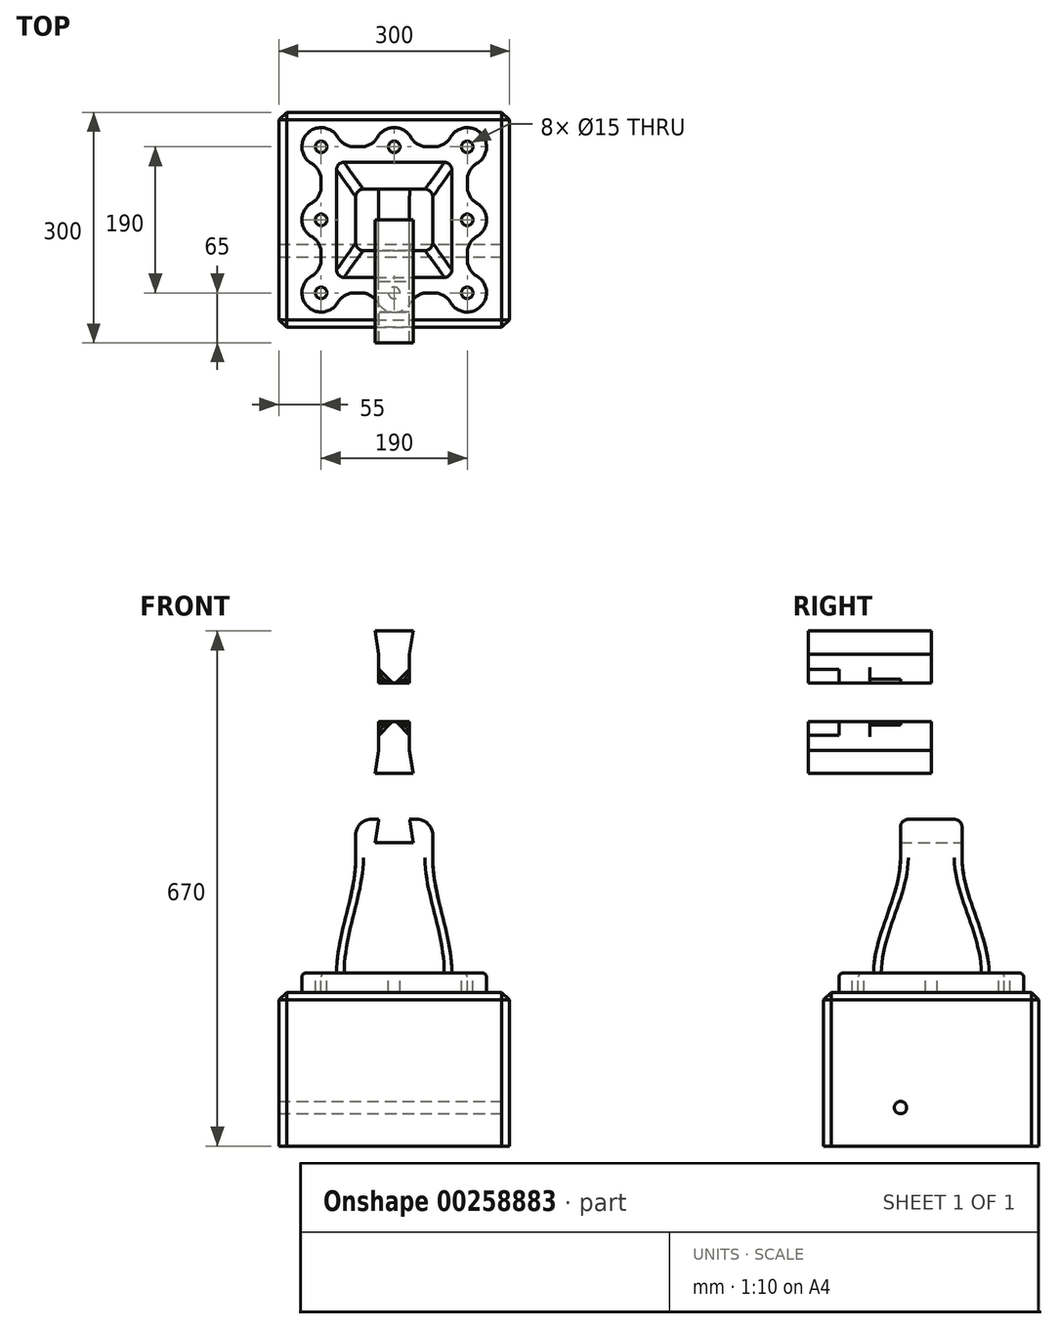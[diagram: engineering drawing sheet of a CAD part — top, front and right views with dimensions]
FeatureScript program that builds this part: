
annotation { "Feature Type Name" : "Feature", "Feature Type Description" : "" }
export const myFeature = defineFeature(function(context is Context, id is Id, definition is map)
    precondition{}
    {
        {
            var Q0;
            Q0=qCreatedBy(makeId("Top.planeOp"),FACE);
            var sketch = newSketch(context, id + "F0", { "sketchPlane" : qUnion([Q0])});
            skLineSegment(sketch, "E0.bottom", {"start": v(-75, 75) * mm, "end": v(75, 75) * mm});
            skLineSegment(sketch, "E0.top", {"start": v(-75, -75) * mm, "end": v(75, -75) * mm});
            skLineSegment(sketch, "E0.left", {"start": v(-75, 75) * mm, "end": v(-75, -75) * mm});
            skLineSegment(sketch, "E0.right", {"start": v(75, 75) * mm, "end": v(75, -75) * mm});
            skPoint(sketch, "E0.middle", {"position": v(0, 0) * mm});
            skCircle(sketch, "E1", {"center": v(-95, 95) * mm, "radius": 7.5 * mm});
            skCircle(sketch, "E2", {"center": v(95, 95) * mm, "radius": 7.5 * mm});
            skCircle(sketch, "E3", {"center": v(95, 0) * mm, "radius": 7.5 * mm});
            skCircle(sketch, "E4", {"center": v(95, -95) * mm, "radius": 7.5 * mm});
            skCircle(sketch, "E5", {"center": v(-95, -95) * mm, "radius": 7.5 * mm});
            skCircle(sketch, "E6", {"center": v(-95, 0) * mm, "radius": 7.5 * mm});
            skArc(sketch, "E7", {"start": v(-107.5, -21.65) * mm, "mid": v(-120, 0) * mm, "end": v(-107.5, 21.65) * mm});
            skArc(sketch, "E8", {"start": v(-107.5, 73.35) * mm, "mid": v(-112.68, 112.68) * mm, "end": v(-73.35, 107.5) * mm});
            skArc(sketch, "E9", {"start": v(73.35, 107.5) * mm, "mid": v(112.68, 112.68) * mm, "end": v(107.5, 73.35) * mm});
            skArc(sketch, "E10", {"start": v(107.5, 21.65) * mm, "mid": v(120, 0) * mm, "end": v(107.5, -21.65) * mm});
            skArc(sketch, "E11", {"start": v(107.5, -73.35) * mm, "mid": v(112.68, -112.68) * mm, "end": v(73.35, -107.5) * mm});
            skArc(sketch, "E12", {"start": v(-73.35, -107.5) * mm, "mid": v(-112.68, -112.68) * mm, "end": v(-107.5, -73.35) * mm});
            skArc(sketch, "E13", {"start": v(-107.5, -73.35) * mm, "mid": v(-98.35, -64.2) * mm, "end": v(-95, -51.7) * mm});
            skLineSegment(sketch, "E14", {"start": v(-95, -51.7) * mm, "end": v(-95, -43.3) * mm});
            skArc(sketch, "E15", {"start": v(-95, -43.3) * mm, "mid": v(-98.35, -30.8) * mm, "end": v(-107.5, -21.65) * mm});
            skArc(sketch, "E16", {"start": v(-107.5, 21.65) * mm, "mid": v(-98.35, 30.8) * mm, "end": v(-95, 43.3) * mm});
            skArc(sketch, "E17", {"start": v(-95, 51.7) * mm, "mid": v(-98.35, 64.2) * mm, "end": v(-107.5, 73.35) * mm});
            skArc(sketch, "E18", {"start": v(-51.7, 95) * mm, "mid": v(-64.2, 98.35) * mm, "end": v(-73.35, 107.5) * mm});
            skArc(sketch, "E19", {"start": v(51.7, 95) * mm, "mid": v(64.2, 98.35) * mm, "end": v(73.35, 107.5) * mm});
            skArc(sketch, "E20", {"start": v(-51.7, -95) * mm, "mid": v(-64.2, -98.35) * mm, "end": v(-73.35, -107.5) * mm});
            skLineSegment(sketch, "E21", {"start": v(-95, 51.7) * mm, "end": v(-95, 43.3) * mm});
            skArc(sketch, "E22", {"start": v(73.35, -107.5) * mm, "mid": v(64.2, -98.35) * mm, "end": v(51.7, -95) * mm});
            skArc(sketch, "E23", {"start": v(95, 43.3) * mm, "mid": v(98.35, 30.8) * mm, "end": v(107.5, 21.65) * mm});
            skArc(sketch, "E24", {"start": v(107.5, 73.35) * mm, "mid": v(98.35, 64.2) * mm, "end": v(95, 51.7) * mm});
            skArc(sketch, "E25", {"start": v(95, -51.7) * mm, "mid": v(98.35, -64.2) * mm, "end": v(107.5, -73.35) * mm});
            skArc(sketch, "E26", {"start": v(107.5, -21.65) * mm, "mid": v(98.35, -30.8) * mm, "end": v(95, -43.3) * mm});
            skLineSegment(sketch, "E27", {"start": v(95, -51.7) * mm, "end": v(95, -43.3) * mm});
            skLineSegment(sketch, "E28", {"start": v(95, 43.3) * mm, "end": v(95, 51.7) * mm});
            skCircle(sketch, "E29", {"center": v(0, -95) * mm, "radius": 7.5 * mm});
            skCircle(sketch, "E30", {"center": v(0, 95) * mm, "radius": 7.5 * mm});
            skArc(sketch, "E31", {"start": v(-21.65, 107.5) * mm, "mid": v(0, 120) * mm, "end": v(21.65, 107.5) * mm});
            skArc(sketch, "E32", {"start": v(-43.3, 95) * mm, "mid": v(-30.8, 98.35) * mm, "end": v(-21.65, 107.5) * mm});
            skArc(sketch, "E33", {"start": v(21.65, 107.5) * mm, "mid": v(30.8, 98.35) * mm, "end": v(43.3, 95) * mm});
            skLineSegment(sketch, "E34", {"start": v(-51.7, 95) * mm, "end": v(-43.3, 95) * mm});
            skLineSegment(sketch, "E35", {"start": v(43.3, 95) * mm, "end": v(51.7, 95) * mm});
            skArc(sketch, "E36", {"start": v(-21.65, -107.5) * mm, "mid": v(0, -120) * mm, "end": v(21.65, -107.5) * mm});
            skArc(sketch, "E37", {"start": v(-21.65, -107.5) * mm, "mid": v(-30.8, -98.35) * mm, "end": v(-43.3, -95) * mm});
            skArc(sketch, "E38", {"start": v(43.3, -95) * mm, "mid": v(30.8, -98.35) * mm, "end": v(21.65, -107.5) * mm});
            skLineSegment(sketch, "E39", {"start": v(-51.7, -95) * mm, "end": v(-43.3, -95) * mm});
            skLineSegment(sketch, "E40", {"start": v(43.3, -95) * mm, "end": v(51.7, -95) * mm});
            skLineSegment(sketch, "E41.bottom", {"start": v(-150, 150) * mm, "end": v(150, 150) * mm});
            skLineSegment(sketch, "E41.top", {"start": v(-150, -150) * mm, "end": v(150, -150) * mm});
            skLineSegment(sketch, "E41.left", {"start": v(-150, 150) * mm, "end": v(-150, -150) * mm});
            skLineSegment(sketch, "E41.right", {"start": v(150, 150) * mm, "end": v(150, -150) * mm});
            skSolve(sketch);
        }
        {
            var Q0;
            Q0=qCreatedBy(makeId("Top.planeOp"),FACE);
            cPlane(context, id + "F1", {"entities" : qUnion([Q0]), "cplaneType" : CPlaneType.OFFSET, "offset" : 150 * mm, "width" : 150 * mm, "height" : 150 * mm});
        }
        {
            var Q0;
            Q0=qCreatedBy(id+"F1.planeOp",FACE);
            var sketch = newSketch(context, id + "F2", { "sketchPlane" : qUnion([Q0])});
            skLineSegment(sketch, "E42.bottom", {"start": v(-50, 40) * mm, "end": v(50, 40) * mm});
            skLineSegment(sketch, "E42.top", {"start": v(-50, -40) * mm, "end": v(50, -40) * mm});
            skLineSegment(sketch, "E42.left", {"start": v(-50, 40) * mm, "end": v(-50, -40) * mm});
            skLineSegment(sketch, "E42.right", {"start": v(50, 40) * mm, "end": v(50, -40) * mm});
            skPoint(sketch, "E42.middle", {"position": v(0, 0) * mm});
            skSolve(sketch);
        }
        {
            var Q0;
            Q0=makeQuery(id+"F2.imprint","IMPRINT",FACE,{"disambiguationData":[TD([[makeQuery(id+"F2.imprint","IMPRINT",EDGE,{"derivedFrom":sQuery(id+"F2.wireOp",EDGE,"E42.bottom")}),-1.0]])]});
            var Q1;
            Q1=makeQuery(id+"F0.imprint","IMPRINT",FACE,{"disambiguationData":[TD([[makeQuery(id+"F0.imprint","IMPRINT",EDGE,{"derivedFrom":sQuery(id+"F0.wireOp",EDGE,"E0.bottom")}),-1.0]])]});
            loft(context, id + "F3", {"startCondition" : LoftEndDerivativeType.NORMAL_TO_PROFILE, "startMagnitude" : 1, "endCondition" : LoftEndDerivativeType.NORMAL_TO_PROFILE, "endMagnitude" : 1, "sheetProfilesArray" : [{ "sheetProfileEntities" : qUnion([Q0]) }, { "sheetProfileEntities" : qUnion([Q1]) }]});
        }
        {
            var Q0;
            Q0=qCreatedBy(makeId("Front.planeOp"),FACE);
            var sketch = newSketch(context, id + "F4", { "sketchPlane" : qUnion([Q0])});
            skLineSegment(sketch, "E43", {"start": v(0, 150) * mm, "end": v(50, 150) * mm});
            skLineSegment(sketch, "E44", {"start": v(50, 150) * mm, "end": v(50, 200) * mm});
            skLineSegment(sketch, "E45", {"start": v(50, 200) * mm, "end": v(20, 200) * mm});
            skLineSegment(sketch, "E46", {"start": v(20, 200) * mm, "end": v(25, 170) * mm});
            skLineSegment(sketch, "E47", {"start": v(25, 170) * mm, "end": v(-25, 170) * mm});
            skLineSegment(sketch, "E48", {"start": v(-25, 170) * mm, "end": v(-20, 200) * mm});
            skLineSegment(sketch, "E49", {"start": v(-20, 200) * mm, "end": v(-50, 200) * mm});
            skLineSegment(sketch, "E50", {"start": v(-50, 200) * mm, "end": v(-50, 150) * mm});
            skLineSegment(sketch, "E51", {"start": v(-50, 150) * mm, "end": v(0, 150) * mm});
            skLineSegment(sketch, "E52", {"start": v(-25, 260) * mm, "end": v(25, 260) * mm});
            skLineSegment(sketch, "E53", {"start": v(25, 260) * mm, "end": v(20, 290) * mm});
            skLineSegment(sketch, "E54", {"start": v(20, 290) * mm, "end": v(-20, 290) * mm, "construction": true});
            skLineSegment(sketch, "E55", {"start": v(-20, 290) * mm, "end": v(-25, 260) * mm});
            skLineSegment(sketch, "E56", {"start": v(-20, 290) * mm, "end": v(-20, 307.5) * mm});
            skLineSegment(sketch, "E57", {"start": v(-20, 307.5) * mm, "end": v(20, 307.5) * mm, "construction": true});
            skLineSegment(sketch, "E58", {"start": v(20, 307.5) * mm, "end": v(20, 290) * mm});
            skLineSegment(sketch, "E59", {"start": v(-20, 290) * mm, "end": v(-70, 290) * mm});
            skLineSegment(sketch, "E60", {"start": v(-70, 290) * mm, "end": v(-70, 415) * mm});
            skLineSegment(sketch, "E61", {"start": v(-70, 415) * mm, "end": v(-20, 415) * mm});
            skLineSegment(sketch, "E62", {"start": v(-70, 352.5) * mm, "end": v(25, 352.5) * mm, "construction": true});
            skArc(sketch, "E63", {"start": v(20, 307.5) * mm, "mid": v(0, 327.5) * mm, "end": v(-20, 307.5) * mm});
            skPoint(sketch, "E64.visualSharp", {"position": v(0, 327.5) * mm});
            skLineSegment(sketch, "E65", {"start": v(-20, 307.5) * mm, "end": v(-20, 322.5) * mm});
            skLineSegment(sketch, "E66", {"start": v(20, 307.5) * mm, "end": v(20, 322.5) * mm});
            skLineSegment(sketch, "E67", {"start": v(20, 322.5) * mm, "end": v(20, 327.5) * mm});
            skLineSegment(sketch, "E68", {"start": v(20, 327.5) * mm, "end": v(-20, 327.5) * mm});
            skLineSegment(sketch, "E69", {"start": v(-20, 327.5) * mm, "end": v(-20, 322.5) * mm});
            skArc(sketch, "E70", {"start": v(20, 322.5) * mm, "mid": v(0, 327.5) * mm, "end": v(-20, 322.5) * mm});
            skArc(sketch, "E71", {"start": v(3.54, 326.04) * mm, "mid": v(0, 327.5) * mm, "end": v(-3.54, 326.04) * mm});
            skLineSegment(sketch, "E72", {"start": v(-3.54, 326.04) * mm, "end": v(-19.88, 309.7) * mm});
            skLineSegment(sketch, "E73", {"start": v(-19.88, 309.7) * mm, "end": v(19.88, 309.7) * mm, "construction": true});
            skLineSegment(sketch, "E74", {"start": v(19.88, 309.7) * mm, "end": v(3.54, 326.04) * mm});
            skLineSegment(sketch, "E75.MirrorCS", {"start": v(20, 382.5) * mm, "end": v(20, 377.5) * mm});
            skArc(sketch, "E76.MirrorCS", {"start": v(3.54, 378.96) * mm, "mid": v(0, 377.5) * mm, "end": v(-3.54, 378.96) * mm});
            skLineSegment(sketch, "E77.MirrorCS", {"start": v(-20, 377.5) * mm, "end": v(-20, 382.5) * mm});
            skPoint(sketch, "E78.MirrorP", {"position": v(0, 377.5) * mm});
            skLineSegment(sketch, "E79.MirrorCS", {"start": v(20, 415) * mm, "end": v(-20, 415) * mm, "construction": true});
            skLineSegment(sketch, "E80.MirrorCS", {"start": v(-20, 397.5) * mm, "end": v(20, 397.5) * mm, "construction": true});
            skArc(sketch, "E81.MirrorCS", {"start": v(20, 382.5) * mm, "mid": v(0, 377.5) * mm, "end": v(-20, 382.5) * mm});
            skLineSegment(sketch, "E82.MirrorCS", {"start": v(-20, 397.5) * mm, "end": v(-20, 382.5) * mm});
            skLineSegment(sketch, "E83.MirrorCS", {"start": v(20, 377.5) * mm, "end": v(-20, 377.5) * mm});
            skLineSegment(sketch, "E84.MirrorCS", {"start": v(-25, 445) * mm, "end": v(25, 445) * mm});
            skLineSegment(sketch, "E85.MirrorCS", {"start": v(-19.88, 395.3) * mm, "end": v(19.88, 395.3) * mm, "construction": true});
            skArc(sketch, "E86.MirrorCS", {"start": v(20, 397.5) * mm, "mid": v(0, 377.5) * mm, "end": v(-20, 397.5) * mm});
            skLineSegment(sketch, "E87.MirrorCS", {"start": v(-3.54, 378.96) * mm, "end": v(-19.88, 395.3) * mm});
            skLineSegment(sketch, "E88.MirrorCS", {"start": v(25, 445) * mm, "end": v(20, 415) * mm});
            skLineSegment(sketch, "E89.MirrorCS", {"start": v(-20, 415) * mm, "end": v(-20, 397.5) * mm});
            skLineSegment(sketch, "E90.MirrorCS", {"start": v(-20, 415) * mm, "end": v(-25, 445) * mm});
            skLineSegment(sketch, "E91.MirrorCS", {"start": v(20, 397.5) * mm, "end": v(20, 382.5) * mm});
            skLineSegment(sketch, "E92.MirrorCS", {"start": v(20, 397.5) * mm, "end": v(20, 415) * mm});
            skLineSegment(sketch, "E93.MirrorCS", {"start": v(19.88, 395.3) * mm, "end": v(3.54, 378.96) * mm});
            skSolve(sketch);
        }
        {
            var Q0;
            Q0=makeQuery(id+"F4.imprint","IMPRINT",FACE,{"disambiguationData":[TD([[makeQuery(id+"F4.imprint","IMPRINT",EDGE,{"derivedFrom":sQuery(id+"F4.wireOp",EDGE,"E43")}),1.0]])]});
            extrude(context, id + "F5", {"entities" : qUnion([Q0]), "operationType" : NewBodyOperationType.ADD, "depth" : 80 * mm, "symmetric" : true});
        }
        {
            var Q0;
            Q0=makeQuery(id+"F0.imprint","IMPRINT",FACE,{"disambiguationData":[TD([[makeQuery(id+"F0.imprint","IMPRINT",EDGE,{"derivedFrom":sQuery(id+"F0.wireOp",EDGE,"E0.bottom")}),-1.0]])]});
            var Q1;
            Q1=makeQuery(id+"F0.imprint","IMPRINT",FACE,{"disambiguationData":[TD([[makeQuery(id+"F0.imprint","IMPRINT",EDGE,{"derivedFrom":sQuery(id+"F0.wireOp",EDGE,"E0.bottom")}),1.0]])]});
            extrude(context, id + "F6", {"entities" : qUnion([Q0, Q1]), "operationType" : NewBodyOperationType.ADD, "oppositeDirection" : true, "depth" : 25 * mm});
        }
        {
            var Q0;
            Q0=makeQuery(id+"F5.opExtrude","SWEPT_EDGE",EDGE,{"disambiguationData":[OSD([sQuery(id+"F4.wireOp",EDGE,"E44"),sQuery(id+"F4.wireOp",EDGE,"E45")])]});
            var Q1;
            Q1=makeQuery(id+"F5.opExtrude","SWEPT_EDGE",EDGE,{"disambiguationData":[OSD([sQuery(id+"F4.wireOp",EDGE,"E49"),sQuery(id+"F4.wireOp",EDGE,"E50")])]});
            fillet(context, id + "F7", {"entities" : qUnion([Q0, Q1]), "radius" : 20 * mm, "tangentPropagation" : true, "allowEdgeOverflow" : false});
        }
        {
            var Q0;
            Q0=makeQuery(id+"F3.opLoft","SWEPT_EDGE",EDGE,{"disambiguationData":[OSD([sQuery(id+"F0.wireOp",EDGE,"E0.bottom"),sQuery(id+"F0.wireOp",EDGE,"E0.right"),sQuery(id+"F2.wireOp",EDGE,"E42.bottom"),sQuery(id+"F2.wireOp",EDGE,"E42.right")])]});
            var Q1;
            Q1=makeQuery(id+"F3.opLoft","SWEPT_EDGE",EDGE,{"disambiguationData":[OSD([sQuery(id+"F0.wireOp",EDGE,"E0.top"),sQuery(id+"F0.wireOp",EDGE,"E0.right"),sQuery(id+"F2.wireOp",EDGE,"E42.top"),sQuery(id+"F2.wireOp",EDGE,"E42.right")])]});
            var Q2;
            Q2=makeQuery(id+"F5.opExtrude","CAP_EDGE",EDGE,{"disambiguationData":[OSD([sQuery(id+"F4.wireOp",EDGE,"E49")])],"isStart":false});
            var Q3;
            Q3=makeQuery(id+"F3.opLoft","SWEPT_EDGE",EDGE,{"disambiguationData":[OSD([sQuery(id+"F0.wireOp",EDGE,"E0.bottom"),sQuery(id+"F0.wireOp",EDGE,"E0.left"),sQuery(id+"F2.wireOp",EDGE,"E42.bottom"),sQuery(id+"F2.wireOp",EDGE,"E42.left")])]});
            fillet(context, id + "F8", {"entities" : qUnion([Q0, Q1, Q2, Q3]), "radius" : 10 * mm, "tangentPropagation" : true, "allowEdgeOverflow" : false});
        }
        {
            var Q0;
            Q0=makeQuery(id+"F6.opExtrude","CAP_EDGE",EDGE,{"disambiguationData":[OSD([sQuery(id+"F0.wireOp",EDGE,"E27")])],"isStart":true});
            var Q1;
            Q1=makeQuery(id+"F3.opLoft","MID_CAP_EDGE",EDGE,{"disambiguationData":[OSD([sQuery(id+"F0.wireOp",EDGE,"E0.bottom"),sQuery(id+"F0.wireOp",EDGE,"E0.top"),sQuery(id+"F0.wireOp",EDGE,"E0.right")])],"capPos":1.0});
            fillet(context, id + "F9", {"entities" : qUnion([Q0, Q1]), "radius" : 5 * mm, "tangentPropagation" : true, "allowEdgeOverflow" : false});
        }
        {
            var Q0;
            Q0=qCreatedBy(makeId("Top.planeOp"),FACE);
            cPlane(context, id + "F10", {"entities" : qUnion([Q0]), "cplaneType" : CPlaneType.OFFSET, "offset" : 25 * mm, "oppositeDirection" : true, "width" : 150 * mm, "height" : 150 * mm});
        }
        {
            var Q0;
            Q0=qCreatedBy(id+"F10.planeOp",FACE);
            var sketch = newSketch(context, id + "F11", { "sketchPlane" : qUnion([Q0])});
            skArc(sketch, "E94.0.0", {"start": v(107.5, -21.65) * mm, "mid": v(98.35, -30.8) * mm, "end": v(95, -43.3) * mm});
            skLineSegment(sketch, "E94.0.1", {"start": v(95, -43.3) * mm, "end": v(95, -51.7) * mm});
            skArc(sketch, "E94.0.2", {"start": v(95, -51.7) * mm, "mid": v(98.35, -64.2) * mm, "end": v(107.5, -73.35) * mm});
            skArc(sketch, "E94.0.3", {"start": v(107.5, -73.35) * mm, "mid": v(112.68, -112.68) * mm, "end": v(73.35, -107.5) * mm});
            skArc(sketch, "E94.0.4", {"start": v(73.35, -107.5) * mm, "mid": v(64.2, -98.35) * mm, "end": v(51.7, -95) * mm});
            skLineSegment(sketch, "E94.0.5", {"start": v(51.7, -95) * mm, "end": v(43.3, -95) * mm});
            skArc(sketch, "E94.0.6", {"start": v(43.3, -95) * mm, "mid": v(30.8, -98.35) * mm, "end": v(21.65, -107.5) * mm});
            skArc(sketch, "E94.0.7", {"start": v(21.65, -107.5) * mm, "mid": v(0, -120) * mm, "end": v(-21.65, -107.5) * mm});
            skArc(sketch, "E94.0.8", {"start": v(-21.65, -107.5) * mm, "mid": v(-30.8, -98.35) * mm, "end": v(-43.3, -95) * mm});
            skLineSegment(sketch, "E94.0.9", {"start": v(-43.3, -95) * mm, "end": v(-51.7, -95) * mm});
            skArc(sketch, "E94.0.10", {"start": v(-51.7, -95) * mm, "mid": v(-64.2, -98.35) * mm, "end": v(-73.35, -107.5) * mm});
            skArc(sketch, "E94.0.11", {"start": v(-73.35, -107.5) * mm, "mid": v(-112.68, -112.68) * mm, "end": v(-107.5, -73.35) * mm});
            skArc(sketch, "E94.0.12", {"start": v(-107.5, -73.35) * mm, "mid": v(-98.35, -64.2) * mm, "end": v(-95, -51.7) * mm});
            skLineSegment(sketch, "E94.0.13", {"start": v(-95, -51.7) * mm, "end": v(-95, -43.3) * mm});
            skArc(sketch, "E94.0.14", {"start": v(-95, -43.3) * mm, "mid": v(-98.35, -30.8) * mm, "end": v(-107.5, -21.65) * mm});
            skArc(sketch, "E94.0.15", {"start": v(-107.5, -21.65) * mm, "mid": v(-120, 0) * mm, "end": v(-107.5, 21.65) * mm});
            skArc(sketch, "E94.0.16", {"start": v(-107.5, 21.65) * mm, "mid": v(-98.35, 30.8) * mm, "end": v(-95, 43.3) * mm});
            skLineSegment(sketch, "E94.0.17", {"start": v(-95, 43.3) * mm, "end": v(-95, 51.7) * mm});
            skArc(sketch, "E94.0.18", {"start": v(-95, 51.7) * mm, "mid": v(-98.35, 64.2) * mm, "end": v(-107.5, 73.35) * mm});
            skArc(sketch, "E94.0.19", {"start": v(-107.5, 73.35) * mm, "mid": v(-112.68, 112.68) * mm, "end": v(-73.35, 107.5) * mm});
            skArc(sketch, "E94.0.20", {"start": v(-73.35, 107.5) * mm, "mid": v(-64.2, 98.35) * mm, "end": v(-51.7, 95) * mm});
            skLineSegment(sketch, "E94.0.21", {"start": v(-51.7, 95) * mm, "end": v(-43.3, 95) * mm});
            skArc(sketch, "E94.0.22", {"start": v(-43.3, 95) * mm, "mid": v(-30.8, 98.35) * mm, "end": v(-21.65, 107.5) * mm});
            skArc(sketch, "E94.0.23", {"start": v(-21.65, 107.5) * mm, "mid": v(0, 120) * mm, "end": v(21.65, 107.5) * mm});
            skArc(sketch, "E94.0.24", {"start": v(21.65, 107.5) * mm, "mid": v(30.8, 98.35) * mm, "end": v(43.3, 95) * mm});
            skLineSegment(sketch, "E94.0.25", {"start": v(43.3, 95) * mm, "end": v(51.7, 95) * mm});
            skArc(sketch, "E94.0.26", {"start": v(51.7, 95) * mm, "mid": v(64.2, 98.35) * mm, "end": v(73.35, 107.5) * mm});
            skArc(sketch, "E94.0.27", {"start": v(73.35, 107.5) * mm, "mid": v(112.68, 112.68) * mm, "end": v(107.5, 73.35) * mm});
            skArc(sketch, "E94.0.28", {"start": v(107.5, 73.35) * mm, "mid": v(98.35, 64.2) * mm, "end": v(95, 51.7) * mm});
            skLineSegment(sketch, "E94.0.29", {"start": v(95, 51.7) * mm, "end": v(95, 43.3) * mm});
            skArc(sketch, "E94.0.30", {"start": v(95, 43.3) * mm, "mid": v(98.35, 30.8) * mm, "end": v(107.5, 21.65) * mm});
            skArc(sketch, "E94.0.31", {"start": v(107.5, 21.65) * mm, "mid": v(120, 0) * mm, "end": v(107.5, -21.65) * mm});
            skCircle(sketch, "E95.0", {"center": v(-95, 95) * mm, "radius": 7.5 * mm});
            skCircle(sketch, "E96.0", {"center": v(0, 95) * mm, "radius": 7.5 * mm});
            skCircle(sketch, "E97.0", {"center": v(95, 95) * mm, "radius": 7.5 * mm});
            skCircle(sketch, "E98.0", {"center": v(95, 0) * mm, "radius": 7.5 * mm});
            skCircle(sketch, "E99.0", {"center": v(95, -95) * mm, "radius": 7.5 * mm});
            skCircle(sketch, "E100.0", {"center": v(0, -95) * mm, "radius": 7.5 * mm});
            skCircle(sketch, "E101.0", {"center": v(-95, -95) * mm, "radius": 7.5 * mm});
            skLineSegment(sketch, "E102.bottom", {"start": v(-150, 140) * mm, "end": v(150, 140) * mm});
            skLineSegment(sketch, "E102.top", {"start": v(-150, -140) * mm, "end": v(150, -140) * mm});
            skLineSegment(sketch, "E102.left", {"start": v(-150, 140) * mm, "end": v(-150, -140) * mm});
            skLineSegment(sketch, "E102.right", {"start": v(150, 140) * mm, "end": v(150, -140) * mm});
            skPoint(sketch, "E102.middle", {"position": v(0, 0) * mm});
            skSolve(sketch);
        }
        {
            var Q0;
            Q0=makeQuery(id+"F11.imprint","IMPRINT",FACE,{"disambiguationData":[TD([[makeQuery(id+"F11.imprint","IMPRINT",EDGE,{"derivedFrom":sQuery(id+"F11.wireOp",EDGE,"E94.0.0")}),1.0]])]});
            var Q1;
            Q1=makeQuery(id+"F11.imprint","IMPRINT",FACE,{"disambiguationData":[TD([[makeQuery(id+"F11.imprint","IMPRINT",EDGE,{"derivedFrom":sQuery(id+"F11.wireOp",EDGE,"E94.0.0")}),-1.0]])]});
            var Q2;
            Q2=makeQuery(id+"F11.imprint","IMPRINT",FACE,{"disambiguationData":[TD([[makeQuery(id+"F11.imprint","IMPRINT",EDGE,{"derivedFrom":sQuery(id+"F11.wireOp",EDGE,"E95.0")}),1.0]])]});
            var Q3;
            Q3=makeQuery(id+"F11.imprint","IMPRINT",FACE,{"disambiguationData":[TD([[makeQuery(id+"F11.imprint","IMPRINT",EDGE,{"derivedFrom":sQuery(id+"F11.wireOp",EDGE,"E96.0")}),1.0]])]});
            var Q4;
            Q4=makeQuery(id+"F11.imprint","IMPRINT",FACE,{"disambiguationData":[TD([[makeQuery(id+"F11.imprint","IMPRINT",EDGE,{"derivedFrom":sQuery(id+"F11.wireOp",EDGE,"E97.0")}),1.0]])]});
            var Q5;
            Q5=makeQuery(id+"F11.imprint","IMPRINT",FACE,{"disambiguationData":[TD([[makeQuery(id+"F11.imprint","IMPRINT",EDGE,{"derivedFrom":sQuery(id+"F11.wireOp",EDGE,"E98.0")}),1.0]])]});
            var Q6;
            Q6=makeQuery(id+"F11.imprint","IMPRINT",FACE,{"disambiguationData":[TD([[makeQuery(id+"F11.imprint","IMPRINT",EDGE,{"derivedFrom":sQuery(id+"F11.wireOp",EDGE,"E99.0")}),1.0]])]});
            var Q7;
            Q7=makeQuery(id+"F11.imprint","IMPRINT",FACE,{"disambiguationData":[TD([[makeQuery(id+"F11.imprint","IMPRINT",EDGE,{"derivedFrom":sQuery(id+"F11.wireOp",EDGE,"E100.0")}),1.0]])]});
            var Q8;
            Q8=makeQuery(id+"F11.imprint","IMPRINT",FACE,{"disambiguationData":[TD([[makeQuery(id+"F11.imprint","IMPRINT",EDGE,{"derivedFrom":sQuery(id+"F11.wireOp",EDGE,"E101.0")}),1.0]])]});
            extrude(context, id + "F12", {"entities" : qUnion([Q0, Q1, Q2, Q3, Q4, Q5, Q6, Q7, Q8]), "oppositeDirection" : true, "depth" : 200 * mm});
        }
        {
            var Q0;
            Q0=makeQuery(id+"F12.opExtrude","CAP_EDGE",EDGE,{"disambiguationData":[OSD([sQuery(id+"F11.wireOp",EDGE,"E102.left")])],"isStart":true});
            var Q1;
            Q1=makeQuery(id+"F12.opExtrude","CAP_EDGE",EDGE,{"disambiguationData":[OSD([sQuery(id+"F11.wireOp",EDGE,"E102.bottom")])],"isStart":true});
            var Q2;
            Q2=makeQuery(id+"F12.opExtrude","CAP_EDGE",EDGE,{"disambiguationData":[OSD([sQuery(id+"F11.wireOp",EDGE,"E102.right")])],"isStart":true});
            var Q3;
            Q3=makeQuery(id+"F12.opExtrude","CAP_EDGE",EDGE,{"disambiguationData":[OSD([sQuery(id+"F11.wireOp",EDGE,"E102.top")])],"isStart":true});
            var Q4;
            Q4=makeQuery(id+"F12.opExtrude","SWEPT_EDGE",EDGE,{"disambiguationData":[OSD([sQuery(id+"F11.wireOp",EDGE,"E102.bottom"),sQuery(id+"F11.wireOp",EDGE,"E102.left")])]});
            var Q5;
            Q5=makeQuery(id+"F12.opExtrude","SWEPT_EDGE",EDGE,{"disambiguationData":[OSD([sQuery(id+"F11.wireOp",EDGE,"E102.top"),sQuery(id+"F11.wireOp",EDGE,"E102.left")])]});
            var Q6;
            Q6=makeQuery(id+"F12.opExtrude","SWEPT_EDGE",EDGE,{"disambiguationData":[OSD([sQuery(id+"F11.wireOp",EDGE,"E102.top"),sQuery(id+"F11.wireOp",EDGE,"E102.right")])]});
            var Q7;
            Q7=makeQuery(id+"F12.opExtrude","SWEPT_EDGE",EDGE,{"disambiguationData":[OSD([sQuery(id+"F11.wireOp",EDGE,"E102.bottom"),sQuery(id+"F11.wireOp",EDGE,"E102.right")])]});
            chamfer(context, id + "F13", {"entities" : qUnion([Q0, Q1, Q2, Q3, Q4, Q5, Q6, Q7]), "width" : 10 * mm, "tangentPropagation" : true});
        }
        {
            var Q0;
            Q0=makeQuery(id+"F4.imprint","IMPRINT",FACE,{"disambiguationData":[TD([[makeQuery(id+"F4.imprint","IMPRINT",EDGE,{"derivedFrom":sQuery(id+"F4.wireOp",EDGE,"E52")}),1.0]])]});
            var Q1;
            Q1=makeQuery(id+"F4.imprint","IMPRINT",FACE,{"disambiguationData":[TD([[makeQuery(id+"F4.imprint","IMPRINT",EDGE,{"derivedFrom":sQuery(id+"F4.wireOp",EDGE,"E84.MirrorCS")}),-1.0]])]});
            extrude(context, id + "F14", {"entities" : qUnion([Q0, Q1]), "depth" : 160 * mm});
        }
        {
            var Q0;
            {var subQ0=sQuery(id+"F4.wireOp",EDGE,"E72");Q0=makeQuery(id+"F4.imprint","IMPRINT",FACE,{"disambiguationData":[TD([[makeQuery(id+"F4.imprint","IMPRINT",EDGE,{"derivedFrom":subQ0}),-1.0]])]});}
            var Q1;
            {var subQ0=sQuery(id+"F4.wireOp",EDGE,"E74");Q1=makeQuery(id+"F4.imprint","IMPRINT",FACE,{"disambiguationData":[TD([[makeQuery(id+"F4.imprint","IMPRINT",EDGE,{"derivedFrom":subQ0}),-1.0]])]});}
            var Q2;
            {var subQ0=sQuery(id+"F4.wireOp",EDGE,"E93.MirrorCS");Q2=makeQuery(id+"F4.imprint","IMPRINT",FACE,{"disambiguationData":[TD([[makeQuery(id+"F4.imprint","IMPRINT",EDGE,{"derivedFrom":subQ0}),1.0]])]});}
            var Q3;
            {var subQ0=sQuery(id+"F4.wireOp",EDGE,"E87.MirrorCS");Q3=makeQuery(id+"F4.imprint","IMPRINT",FACE,{"disambiguationData":[TD([[makeQuery(id+"F4.imprint","IMPRINT",EDGE,{"derivedFrom":subQ0}),1.0]])]});}
            extrude(context, id + "F15", {"entities" : qUnion([Q0, Q1, Q2, Q3]), "operationType" : NewBodyOperationType.ADD, "depth" : 120 * mm});
        }
        {
            var Q0;
            {var subQ4=sQuery(id+"F4.wireOp",EDGE,"E65");Q0=makeQuery(id+"F4.imprint","IMPRINT",FACE,{"disambiguationData":[TD([[makeQuery(id+"F4.imprint","IMPRINT",EDGE,{"derivedFrom":subQ4}),-1.0]])]});}
            var Q1;
            {var subQ0=sQuery(id+"F4.wireOp",EDGE,"E66");Q1=makeQuery(id+"F4.imprint","IMPRINT",FACE,{"disambiguationData":[TD([[makeQuery(id+"F4.imprint","IMPRINT",EDGE,{"derivedFrom":subQ0}),1.0]])]});}
            var Q2;
            {var subQ0=sQuery(id+"F4.wireOp",EDGE,"E82.MirrorCS");Q2=makeQuery(id+"F4.imprint","IMPRINT",FACE,{"disambiguationData":[TD([[makeQuery(id+"F4.imprint","IMPRINT",EDGE,{"derivedFrom":subQ0}),1.0]])]});}
            var Q3;
            {var subQ0=sQuery(id+"F4.wireOp",EDGE,"E91.MirrorCS");Q3=makeQuery(id+"F4.imprint","IMPRINT",FACE,{"disambiguationData":[TD([[makeQuery(id+"F4.imprint","IMPRINT",EDGE,{"derivedFrom":subQ0}),-1.0]])]});}
            extrude(context, id + "F16", {"entities" : qUnion([Q0, Q1, Q2, Q3]), "operationType" : NewBodyOperationType.ADD, "depth" : 80 * mm});
        }
        {
            var Q0;
            {var subQ0=sQuery(id+"F4.wireOp",EDGE,"E67");Q0=makeQuery(id+"F4.imprint","IMPRINT",FACE,{"disambiguationData":[TD([[makeQuery(id+"F4.imprint","IMPRINT",EDGE,{"derivedFrom":subQ0}),1.0]])]});}
            var Q1;
            {var subQ0=sQuery(id+"F4.wireOp",EDGE,"E69");Q1=makeQuery(id+"F4.imprint","IMPRINT",FACE,{"disambiguationData":[TD([[makeQuery(id+"F4.imprint","IMPRINT",EDGE,{"derivedFrom":subQ0}),1.0]])]});}
            var Q2;
            {var subQ0=sQuery(id+"F4.wireOp",EDGE,"E77.MirrorCS");Q2=makeQuery(id+"F4.imprint","IMPRINT",FACE,{"disambiguationData":[TD([[makeQuery(id+"F4.imprint","IMPRINT",EDGE,{"derivedFrom":subQ0}),-1.0]])]});}
            var Q3;
            {var subQ0=sQuery(id+"F4.wireOp",EDGE,"E75.MirrorCS");Q3=makeQuery(id+"F4.imprint","IMPRINT",FACE,{"disambiguationData":[TD([[makeQuery(id+"F4.imprint","IMPRINT",EDGE,{"derivedFrom":subQ0}),-1.0]])]});}
            extrude(context, id + "F17", {"entities" : qUnion([Q0, Q1, Q2, Q3]), "operationType" : NewBodyOperationType.ADD, "depth" : 40 * mm});
        }
        {
            var Q0;
            Q0=qCreatedBy(makeId("Right.planeOp"),FACE);
            var sketch = newSketch(context, id + "F18", { "sketchPlane" : qUnion([Q0])});
            skCircle(sketch, "E103", {"center": v(-40, -175) * mm, "radius": 8 * mm});
            skLineSegment(sketch, "E104.0.1", {"start": v(-140, -225) * mm, "end": v(-140, -35) * mm});
            skLineSegment(sketch, "E104.0.3", {"start": v(-140, -35) * mm, "end": v(-140, -225) * mm});
            skSolve(sketch);
        }
        {
            var Q0;
            Q0 = qSketchRegion(id + "F18", true);
            extrude(context, id + "F19", {"entities" : qUnion([Q0]), "operationType" : NewBodyOperationType.REMOVE, "oppositeDirection" : true, "depth" : 478 * mm, "symmetric" : true});
        }
    });
